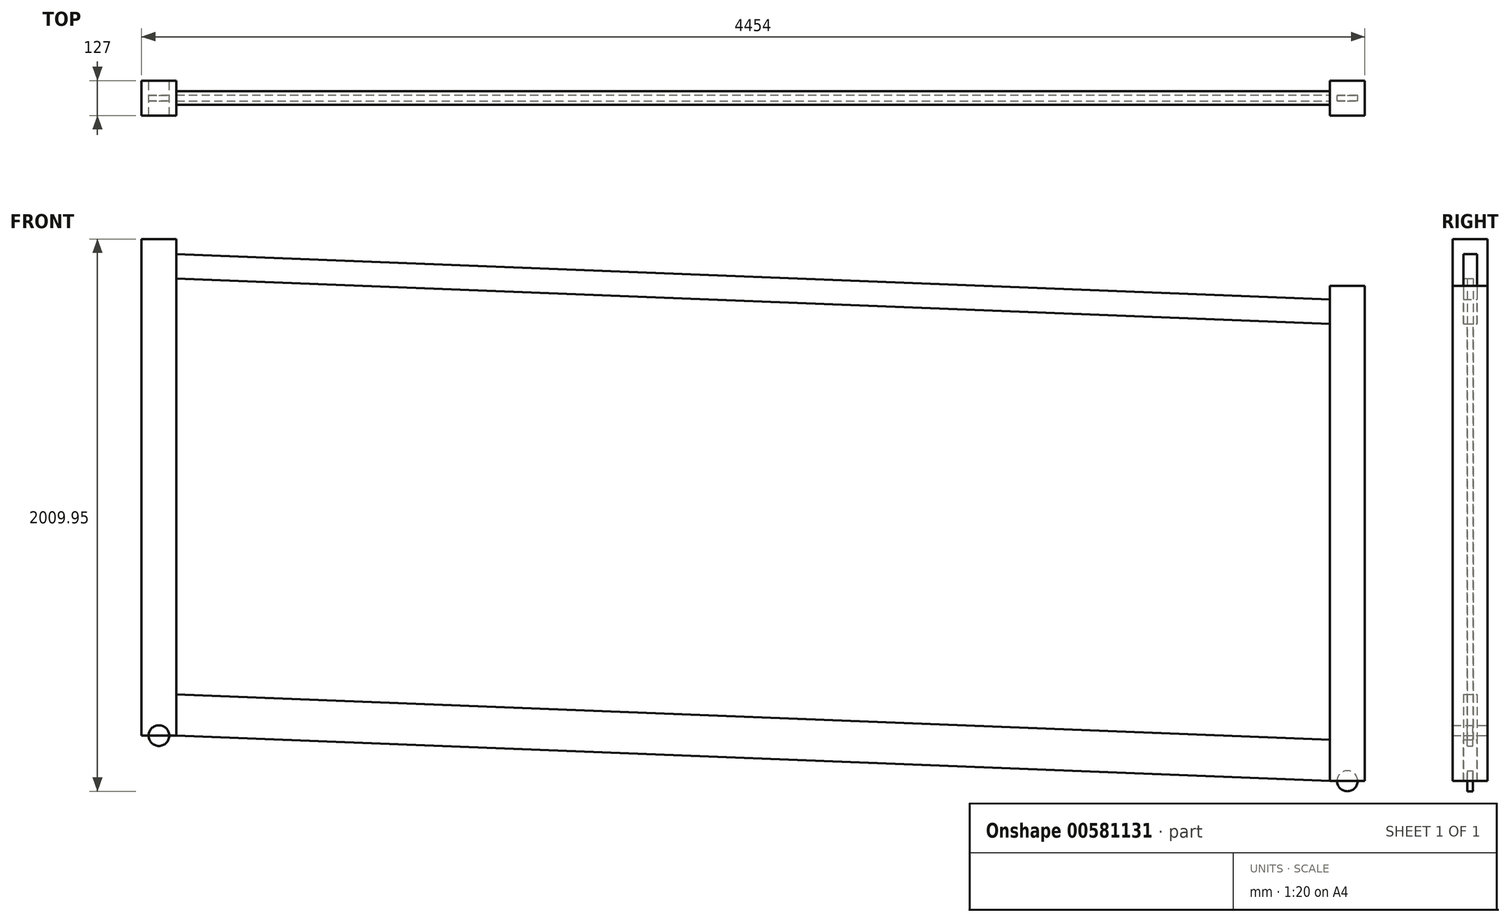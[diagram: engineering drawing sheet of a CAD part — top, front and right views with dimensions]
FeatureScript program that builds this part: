
annotation { "Feature Type Name" : "Feature", "Feature Type Description" : "" }
export const myFeature = defineFeature(function(context is Context, id is Id, definition is map)
    precondition{}
    {
        {
            var Q0;
            Q0=qCreatedBy(makeId("Front.planeOp"),FACE);
            var sketch = newSketch(context, id + "F0", { "sketchPlane" : qUnion([Q0])});
            skLineSegment(sketch, "E0", {"start": v(2015.76, -416.18) * mm, "end": v(2015.76, -413.68) * mm});
            skLineSegment(sketch, "E1", {"start": v(2015.76, 1438.81) * mm, "end": v(2142.76, 1438.81) * mm});
            skLineSegment(sketch, "E2", {"start": v(2142.76, 1438.81) * mm, "end": v(2142.76, -363.64) * mm});
            skLineSegment(sketch, "E3", {"start": v(-2311.24, 1608.81) * mm, "end": v(-2184.24, 1608.81) * mm});
            skLineSegment(sketch, "E4.left", {"start": v(-2311.24, 1608.81) * mm, "end": v(-2311.24, -198.63) * mm});
            skLineSegment(sketch, "E4.right", {"start": v(-2184.24, 1603.82) * mm, "end": v(-2184.24, -198.63) * mm});
            skLineSegment(sketch, "E5", {"start": v(-2247.74, -246.18) * mm, "end": v(2079.26, -416.18) * mm});
            skLineSegment(sketch, "E6", {"start": v(2079.26, -416.18) * mm, "end": v(6691.13, -597.37) * mm});
            skLineSegment(sketch, "E7", {"start": v(-2247.74, -246.18) * mm, "end": v(-3590.13, -193.44) * mm});
            skLineSegment(sketch, "E8", {"start": v(-2184.24, -198.63) * mm, "end": v(2015.76, -363.64) * mm});
            skLineSegment(sketch, "E9", {"start": v(-2184.24, 1553.82) * mm, "end": v(2015.76, 1388.81) * mm});
            skLineSegment(sketch, "E10", {"start": v(-2184.24, 1465.75) * mm, "end": v(2015.76, 1300.74) * mm});
            skLineSegment(sketch, "E11", {"start": v(-2184.24, -48.52) * mm, "end": v(2015.76, -213.53) * mm});
            skLineSegment(sketch, "E12", {"start": v(-2184.24, -198.63) * mm, "end": v(-2311.24, -198.63) * mm});
            skCircle(sketch, "E13", {"center": v(-2247.74, -198.63) * mm, "radius": 37.5 * mm});
            skLineSegment(sketch, "E14", {"start": v(2015.76, -363.64) * mm, "end": v(2142.76, -363.64) * mm});
            skCircle(sketch, "E15", {"center": v(2079.26, -363.64) * mm, "radius": 37.5 * mm});
            skLineSegment(sketch, "E16.trimOffspring", {"start": v(-2311.24, -243.68) * mm, "end": v(-2311.24, -246.18) * mm});
            skPoint(sketch, "E17.orphan", {"position": v(-2184.24, -246.18) * mm});
            skLineSegment(sketch, "E18.trimOffspring", {"start": v(2015.76, -363.64) * mm, "end": v(2015.76, 1438.81) * mm});
            skPoint(sketch, "E19.orphan", {"position": v(2142.76, -416.18) * mm});
            skLineSegment(sketch, "E20", {"start": v(-4396.98, -74.07) * mm, "end": v(-4396.98, 0) * mm});
            skLineSegment(sketch, "E21", {"start": v(-4768.67, 1608.81) * mm, "end": v(4988.26, 1608.81) * mm});
            skLineSegment(sketch, "E22", {"start": v(-2184.24, 1603.82) * mm, "end": v(-2184.24, 1608.81) * mm});
            skSolve(sketch);
        }
        {
            var Q0;
            {var subQ1=sQuery(id+"F0.wireOp",EDGE,"E4.bottom");Q0=makeQuery(id+"F0.imprint","IMPRINT",FACE,{"disambiguationData":[TD([[makeQuery(id+"F0.imprint","IMPRINT",EDGE,{"derivedFrom":subQ1}),-1.0]])]});}
            var Q1;
            {var subQ7=sQuery(id+"F0.wireOp",EDGE,"E1");Q1=makeQuery(id+"F0.imprint","IMPRINT",FACE,{"disambiguationData":[TD([[makeQuery(id+"F0.imprint","IMPRINT",EDGE,{"derivedFrom":subQ7}),-1.0]])]});}
            var Q2;
            {var subQ0=sQuery(id+"F0.wireOp",EDGE,"E13");var subQ1=sQuery(id+"F0.wireOp",EDGE,"E12");var subQ2=makeQuery(id+"F0.imprint","INTERSECT",VERTEX,{"disambiguationData":[OD(0.0)],"derivedFrom":[subQ1,subQ0]});Q2=makeQuery(id+"F0.imprint","IMPRINT",FACE,{"disambiguationData":[TD([[makeQuery(id+"F0.imprint","IMPRINT",EDGE,{"disambiguationData":[TD([[subQ2,-1.0]])],"derivedFrom":subQ1}),-1.0]])]});}
            var Q3;
            {var subQ0=sQuery(id+"F0.wireOp",EDGE,"E15");var subQ1=sQuery(id+"F0.wireOp",EDGE,"E14");var subQ2=makeQuery(id+"F0.imprint","INTERSECT",VERTEX,{"disambiguationData":[OD(0.0)],"derivedFrom":[subQ1,subQ0]});Q3=makeQuery(id+"F0.imprint","IMPRINT",FACE,{"disambiguationData":[TD([[makeQuery(id+"F0.imprint","IMPRINT",EDGE,{"disambiguationData":[TD([[subQ2,-1.0]])],"derivedFrom":subQ1}),1.0]])]});}
            extrude(context, id + "F1", {"entities" : qUnion([Q0, Q1, Q2, Q3]), "oppositeDirection" : true, "depth" : 63.5 * mm, "offsetDistance" : 25 * mm, "hasSecondDirection" : true, "secondDirectionOppositeDirection" : false, "secondDirectionDepth" : 63.5 * mm});
        }
        {
            var Q0;
            {var subQ0=sQuery(id+"F0.wireOp",EDGE,"E13");var subQ1=sQuery(id+"F0.wireOp",EDGE,"E12");var subQ2=makeQuery(id+"F0.imprint","INTERSECT",VERTEX,{"disambiguationData":[OD(0.0)],"derivedFrom":[subQ1,subQ0]});Q0=makeQuery(id+"F0.imprint","IMPRINT",FACE,{"disambiguationData":[TD([[makeQuery(id+"F0.imprint","IMPRINT",EDGE,{"disambiguationData":[TD([[subQ2,-1.0]])],"derivedFrom":subQ1}),1.0]])]});}
            var Q1;
            {var subQ0=sQuery(id+"F0.wireOp",EDGE,"E13");var subQ1=sQuery(id+"F0.wireOp",EDGE,"E12");var subQ2=makeQuery(id+"F0.imprint","INTERSECT",VERTEX,{"disambiguationData":[OD(0.0)],"derivedFrom":[subQ1,subQ0]});Q1=makeQuery(id+"F0.imprint","IMPRINT",FACE,{"disambiguationData":[TD([[makeQuery(id+"F0.imprint","IMPRINT",EDGE,{"disambiguationData":[TD([[subQ2,-1.0]])],"derivedFrom":subQ1}),-1.0]])]});}
            var Q2;
            {var subQ0=sQuery(id+"F0.wireOp",EDGE,"E15");var subQ1=sQuery(id+"F0.wireOp",EDGE,"E14");var subQ2=makeQuery(id+"F0.imprint","INTERSECT",VERTEX,{"disambiguationData":[OD(0.0)],"derivedFrom":[subQ1,subQ0]});Q2=makeQuery(id+"F0.imprint","IMPRINT",FACE,{"disambiguationData":[TD([[makeQuery(id+"F0.imprint","IMPRINT",EDGE,{"disambiguationData":[TD([[subQ2,-1.0]])],"derivedFrom":subQ1}),1.0]])]});}
            var Q3;
            {var subQ0=sQuery(id+"F0.wireOp",EDGE,"E15");var subQ1=sQuery(id+"F0.wireOp",EDGE,"E14");var subQ2=makeQuery(id+"F0.imprint","INTERSECT",VERTEX,{"disambiguationData":[OD(0.0)],"derivedFrom":[subQ1,subQ0]});Q3=makeQuery(id+"F0.imprint","IMPRINT",FACE,{"disambiguationData":[TD([[makeQuery(id+"F0.imprint","IMPRINT",EDGE,{"disambiguationData":[TD([[subQ2,-1.0]])],"derivedFrom":subQ1}),-1.0]])]});}
            extrude(context, id + "F2", {"entities" : qUnion([Q0, Q1, Q2, Q3]), "depth" : 10 * mm, "offsetDistance" : 25 * mm, "hasSecondDirection" : true, "secondDirectionOppositeDirection" : true, "secondDirectionDepth" : 10 * mm});
        }
        {
            var Q0;
            {var subQ0=sQuery(id+"F0.wireOp",EDGE,"E8");Q0=makeQuery(id+"F0.imprint","IMPRINT",FACE,{"disambiguationData":[TD([[makeQuery(id+"F0.imprint","IMPRINT",EDGE,{"derivedFrom":subQ0}),1.0]])]});}
            var Q1;
            {var subQ0=sQuery(id+"F0.wireOp",EDGE,"E9");Q1=makeQuery(id+"F0.imprint","IMPRINT",FACE,{"disambiguationData":[TD([[makeQuery(id+"F0.imprint","IMPRINT",EDGE,{"derivedFrom":subQ0}),-1.0]])]});}
            extrude(context, id + "F3", {"entities" : qUnion([Q0, Q1]), "depth" : 25 * mm, "offsetDistance" : 25 * mm, "hasSecondDirection" : true, "secondDirectionOppositeDirection" : true, "secondDirectionDepth" : 25 * mm});
        }
        {
            var Q0;
            {var subQ0=sQuery(id+"F0.wireOp",EDGE,"E10");Q0=makeQuery(id+"F0.imprint","IMPRINT",FACE,{"disambiguationData":[TD([[makeQuery(id+"F0.imprint","IMPRINT",EDGE,{"derivedFrom":subQ0}),-1.0]])]});}
            extrude(context, id + "F4", {"entities" : qUnion([Q0]), "depth" : 11 * mm, "offsetDistance" : 25 * mm, "hasSecondDirection" : true, "secondDirectionOppositeDirection" : true, "secondDirectionDepth" : 11 * mm});
        }
        {
            var Q0;
            {var subQ10=sQuery(id+"F0.wireOp",EDGE,"E4.left");Q0=makeQuery(id+"F0.imprint","IMPRINT",FACE,{"disambiguationData":[TD([[makeQuery(id+"F0.imprint","IMPRINT",EDGE,{"derivedFrom":subQ10}),1.0]])]});}
            extrude(context, id + "F5", {"entities" : qUnion([Q0]), "depth" : 63.5 * mm, "offsetDistance" : 25 * mm, "hasSecondDirection" : true, "secondDirectionOppositeDirection" : true, "secondDirectionDepth" : 63.5 * mm});
        }
    });
